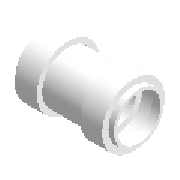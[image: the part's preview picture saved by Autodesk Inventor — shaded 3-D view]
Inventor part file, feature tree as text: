
AUTODESK INVENTOR PART (.ipt)
format: ipt  version: 2023.1 (Build 271208000, 208)  size: 200,192 bytes
history: native  units: mm (DEFAULTED — no unit token found)
features: other x8, revolve x1, sketch x1
ambient origin geometry x8: Origin, YZ Plane, XZ Plane, XY Plane, X Axis, Y Axis, Z Axis, Center Point
bodies: Solid1 (feature_tree)
feature tree (10):
  revolve  "Revolution1"  [1 undecoded]
  other  "Work Point1"
  other  "Work Point2"
  other  "Work Axis1"
  other  "Work Point3"
  other  "Work Axis2"
  other  "Work Point4"
  other  "Work Axis3"
  other  "Work Axis4"
  sketch  "Sketch1"  dims[d0=2.4mm d1=2.4mm d2=2.4mm d3=2.4mm d4=32.0mm d69=90.0deg d5=84.0mm d6=160.5mm d7=3.2mm d8=7.2mm d9=11.2mm]
note: 1 required parameter value undecoded (feature->parameter linkage not recoverable at this tier; creation-order binding heuristic only, values carry confidence <= 0.55)
